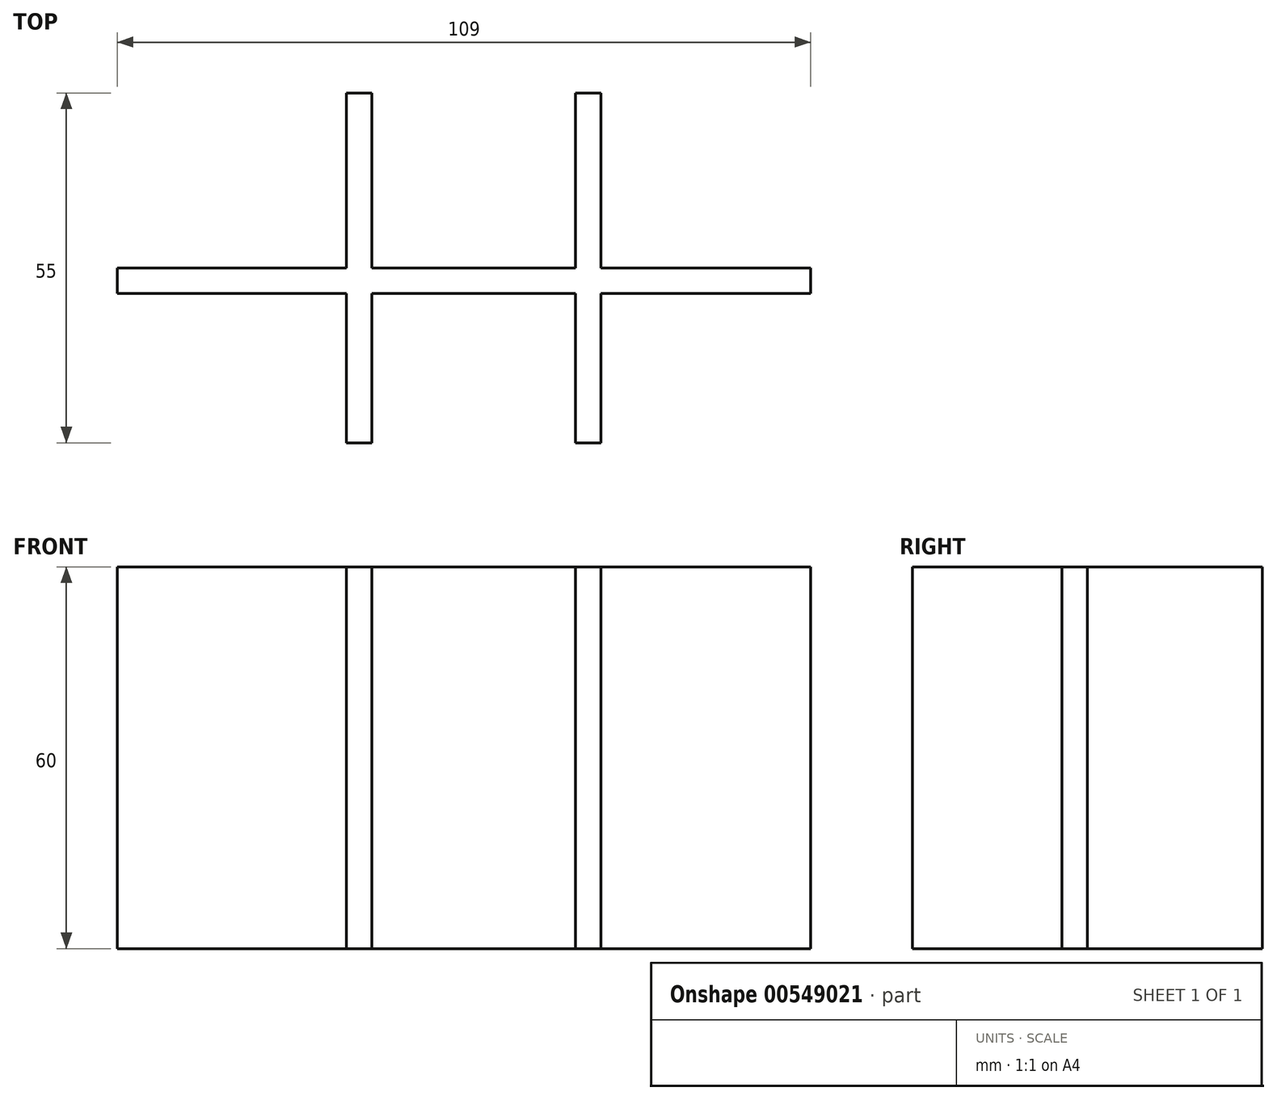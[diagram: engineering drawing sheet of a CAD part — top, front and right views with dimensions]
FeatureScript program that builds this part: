
annotation { "Feature Type Name" : "Feature", "Feature Type Description" : "" }
export const myFeature = defineFeature(function(context is Context, id is Id, definition is map)
    precondition{}
    {
        {
            var Q0;
            Q0=qCreatedBy(makeId("Top.planeOp"),FACE);
            var sketch = newSketch(context, id + "F0", { "sketchPlane" : qUnion([Q0])});
            skLineSegment(sketch, "E0.bottom", {"start": v(-45.82, 11.09) * mm, "end": v(63.18, 11.09) * mm});
            skLineSegment(sketch, "E0.top", {"start": v(-45.82, 7.09) * mm, "end": v(63.18, 7.09) * mm});
            skLineSegment(sketch, "E0.left", {"start": v(-45.82, 11.09) * mm, "end": v(-45.82, 7.09) * mm});
            skLineSegment(sketch, "E0.right", {"start": v(63.18, 11.09) * mm, "end": v(63.18, 7.09) * mm});
            skLineSegment(sketch, "E1", {"start": v(-45.82, 11.09) * mm, "end": v(-9.82, 11.09) * mm});
            skLineSegment(sketch, "E2", {"start": v(-9.82, 11.09) * mm, "end": v(26.18, 11.09) * mm});
            skLineSegment(sketch, "E3.bottom", {"start": v(-9.82, 11.09) * mm, "end": v(-5.82, 11.09) * mm});
            skLineSegment(sketch, "E3.top", {"start": v(-9.82, 38.59) * mm, "end": v(-5.82, 38.59) * mm});
            skLineSegment(sketch, "E3.left", {"start": v(-9.82, 11.09) * mm, "end": v(-9.82, 38.59) * mm});
            skLineSegment(sketch, "E3.right", {"start": v(-5.82, 11.09) * mm, "end": v(-5.82, 38.59) * mm});
            skLineSegment(sketch, "E4.top", {"start": v(-9.82, -16.41) * mm, "end": v(-5.82, -16.41) * mm});
            skLineSegment(sketch, "E4.left", {"start": v(-9.82, 11.09) * mm, "end": v(-9.82, -16.41) * mm});
            skLineSegment(sketch, "E4.right", {"start": v(-5.82, 11.09) * mm, "end": v(-5.82, -16.41) * mm});
            skLineSegment(sketch, "E5.bottom", {"start": v(26.18, 11.09) * mm, "end": v(30.18, 11.09) * mm});
            skLineSegment(sketch, "E5.top", {"start": v(26.18, 38.59) * mm, "end": v(30.18, 38.59) * mm});
            skLineSegment(sketch, "E5.left", {"start": v(26.18, 11.09) * mm, "end": v(26.18, 38.59) * mm});
            skLineSegment(sketch, "E5.right", {"start": v(30.18, 11.09) * mm, "end": v(30.18, 38.59) * mm});
            skLineSegment(sketch, "E6.top", {"start": v(26.18, -16.41) * mm, "end": v(30.18, -16.41) * mm});
            skLineSegment(sketch, "E6.left", {"start": v(26.18, 11.09) * mm, "end": v(26.18, -16.41) * mm});
            skLineSegment(sketch, "E6.right", {"start": v(30.18, 11.09) * mm, "end": v(30.18, -16.41) * mm});
            skSolve(sketch);
        }
        {
            var Q0;
            Q0=makeQuery(id+"F0.imprint","IMPRINT",FACE,{"disambiguationData":[TD([[makeQuery(id+"F0.imprint","IMPRINT",EDGE,{"derivedFrom":sQuery(id+"F0.wireOp",EDGE,"E3.top")}),-1.0]])]});
            var Q1;
            {var subQ5=sQuery(id+"F0.wireOp",EDGE,"E3.bottom");Q1=makeQuery(id+"F0.imprint","IMPRINT",FACE,{"disambiguationData":[TD([[makeQuery(id+"F0.imprint","IMPRINT",EDGE,{"derivedFrom":subQ5}),-1.0]])]});}
            var Q2;
            {var subQ0=sQuery(id+"F0.wireOp",EDGE,"E0.left");Q2=makeQuery(id+"F0.imprint","IMPRINT",FACE,{"disambiguationData":[TD([[makeQuery(id+"F0.imprint","IMPRINT",EDGE,{"derivedFrom":subQ0}),1.0]])]});}
            var Q3;
            {var subQ5=sQuery(id+"F0.wireOp",EDGE,"E4.top");Q3=makeQuery(id+"F0.imprint","IMPRINT",FACE,{"disambiguationData":[TD([[makeQuery(id+"F0.imprint","IMPRINT",EDGE,{"derivedFrom":subQ5}),1.0]])]});}
            var Q4;
            {var subQ5=sQuery(id+"F0.wireOp",EDGE,"E2");Q4=makeQuery(id+"F0.imprint","IMPRINT",FACE,{"disambiguationData":[TD([[makeQuery(id+"F0.imprint","IMPRINT",EDGE,{"derivedFrom":subQ5}),-1.0]])]});}
            var Q5;
            Q5=makeQuery(id+"F0.imprint","IMPRINT",FACE,{"disambiguationData":[TD([[makeQuery(id+"F0.imprint","IMPRINT",EDGE,{"derivedFrom":sQuery(id+"F0.wireOp",EDGE,"E5.top")}),-1.0]])]});
            var Q6;
            {var subQ0=sQuery(id+"F0.wireOp",EDGE,"E0.bottom");Q6=makeQuery(id+"F0.imprint","IMPRINT",FACE,{"disambiguationData":[TD([[makeQuery(id+"F0.imprint","IMPRINT",EDGE,{"derivedFrom":subQ0}),-1.0]])]});}
            var Q7;
            {var subQ5=sQuery(id+"F0.wireOp",EDGE,"E6.top");Q7=makeQuery(id+"F0.imprint","IMPRINT",FACE,{"disambiguationData":[TD([[makeQuery(id+"F0.imprint","IMPRINT",EDGE,{"derivedFrom":subQ5}),1.0]])]});}
            var Q8;
            {var subQ5=sQuery(id+"F0.wireOp",EDGE,"E5.bottom");Q8=makeQuery(id+"F0.imprint","IMPRINT",FACE,{"disambiguationData":[TD([[makeQuery(id+"F0.imprint","IMPRINT",EDGE,{"derivedFrom":subQ5}),-1.0]])]});}
            extrude(context, id + "F1", {"entities" : qUnion([Q0, Q1, Q2, Q3, Q4, Q5, Q6, Q7, Q8]), "depth" : 60 * mm, "offsetDistance" : 25 * mm});
        }
    });
